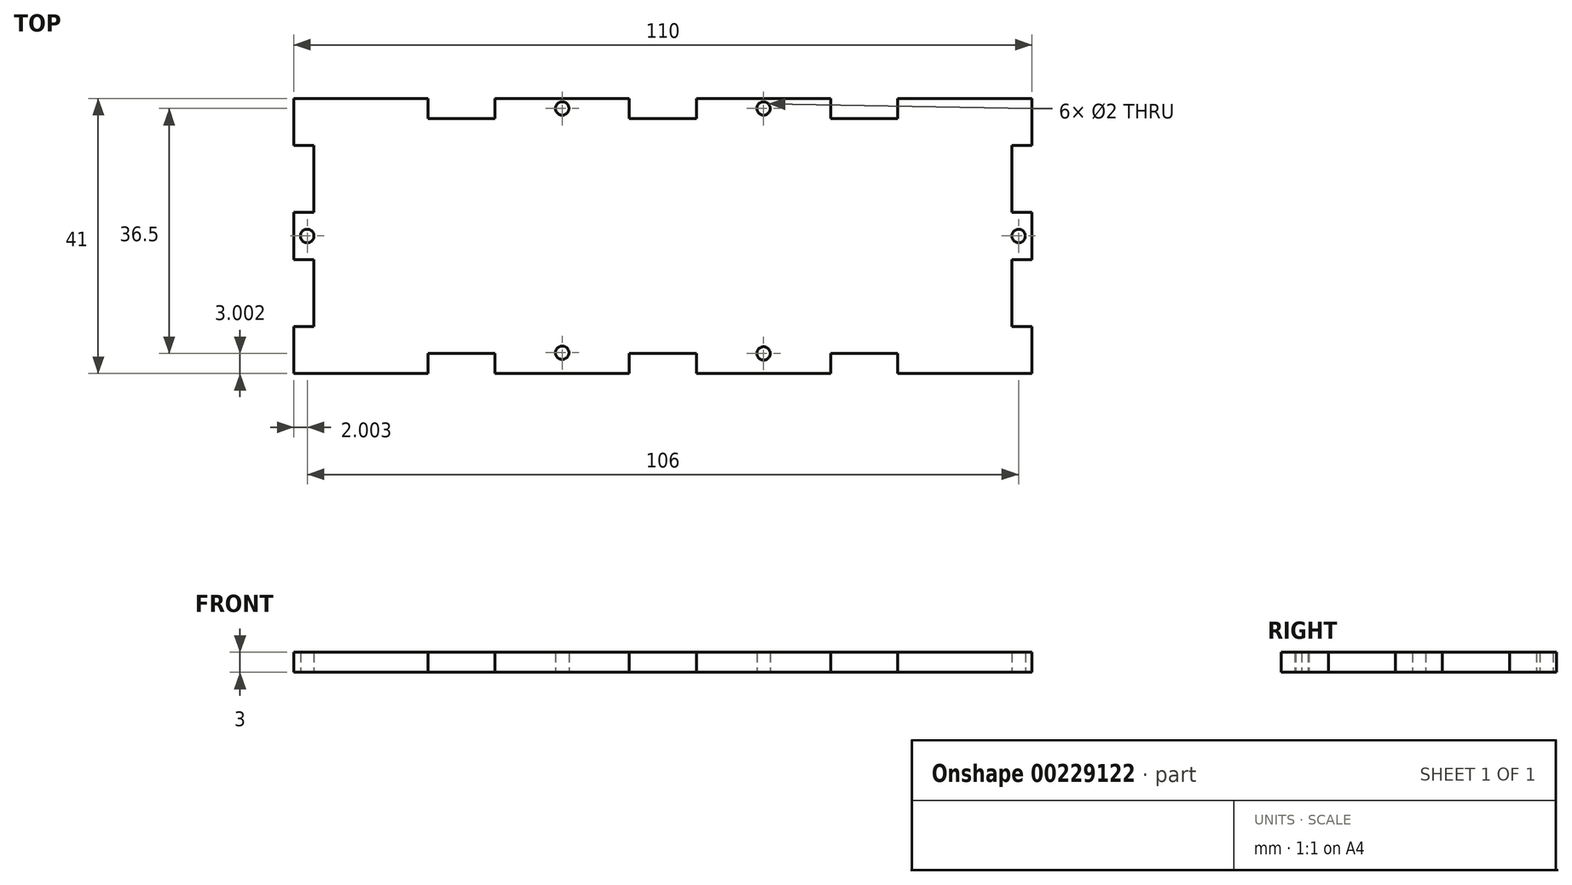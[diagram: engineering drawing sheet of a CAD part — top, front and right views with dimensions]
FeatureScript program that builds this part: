
annotation { "Feature Type Name" : "Feature", "Feature Type Description" : "" }
export const myFeature = defineFeature(function(context is Context, id is Id, definition is map)
    precondition{}
    {
        {
            var Q0;
            Q0=qCreatedBy(makeId("Top.planeOp"),FACE);
            var sketch = newSketch(context, id + "F0", { "sketchPlane" : qUnion([Q0])});
            skLineSegment(sketch, "E0", {"start": v(-52.05, -22.33) * mm, "end": v(-52.05, -15.33) * mm});
            skLineSegment(sketch, "E1", {"start": v(-52.05, -15.33) * mm, "end": v(-49.05, -15.33) * mm});
            skLineSegment(sketch, "E2", {"start": v(-49.05, -15.33) * mm, "end": v(-49.05, -5.33) * mm});
            skLineSegment(sketch, "E3", {"start": v(-49.05, -5.33) * mm, "end": v(-52.05, -5.33) * mm});
            skLineSegment(sketch, "E4", {"start": v(-52.05, -5.33) * mm, "end": v(-52.05, 1.67) * mm});
            skLineSegment(sketch, "E5", {"start": v(-52.05, 1.67) * mm, "end": v(-49.05, 1.67) * mm});
            skLineSegment(sketch, "E6", {"start": v(-49.05, 1.67) * mm, "end": v(-49.05, 11.67) * mm});
            skLineSegment(sketch, "E7", {"start": v(-49.05, 11.67) * mm, "end": v(-52.05, 11.67) * mm});
            skLineSegment(sketch, "E8", {"start": v(-52.05, 11.67) * mm, "end": v(-52.05, 18.67) * mm});
            skLineSegment(sketch, "E9", {"start": v(-52.05, -22.33) * mm, "end": v(-32.05, -22.33) * mm});
            skLineSegment(sketch, "E10", {"start": v(-32.05, -22.33) * mm, "end": v(-32.05, -19.33) * mm});
            skLineSegment(sketch, "E11", {"start": v(-32.05, -19.33) * mm, "end": v(-22.05, -19.33) * mm});
            skLineSegment(sketch, "E12", {"start": v(-22.05, -19.33) * mm, "end": v(-22.05, -22.33) * mm});
            skLineSegment(sketch, "E13", {"start": v(-22.05, -22.33) * mm, "end": v(-2.05, -22.33) * mm});
            skLineSegment(sketch, "E14", {"start": v(-2.05, -22.33) * mm, "end": v(-2.05, -19.33) * mm});
            skLineSegment(sketch, "E15", {"start": v(-2.05, -19.33) * mm, "end": v(2.95, -19.33) * mm});
            skLineSegment(sketch, "E16", {"start": v(-52.05, -1.83) * mm, "end": v(2.95, -1.83) * mm, "construction": true});
            skLineSegment(sketch, "E17.MirrorCS", {"start": v(-22.05, 15.67) * mm, "end": v(-22.05, 18.67) * mm});
            skLineSegment(sketch, "E18.MirrorCS", {"start": v(-32.05, 15.67) * mm, "end": v(-22.05, 15.67) * mm});
            skLineSegment(sketch, "E19.MirrorCS", {"start": v(-32.05, 18.67) * mm, "end": v(-32.05, 15.67) * mm});
            skLineSegment(sketch, "E20.MirrorCS", {"start": v(-2.05, 15.67) * mm, "end": v(2.95, 15.67) * mm});
            skLineSegment(sketch, "E21.MirrorCS", {"start": v(-52.05, 18.67) * mm, "end": v(-32.05, 18.67) * mm});
            skLineSegment(sketch, "E22.MirrorCS", {"start": v(-2.05, 18.67) * mm, "end": v(-2.05, 15.67) * mm});
            skLineSegment(sketch, "E23.MirrorCS", {"start": v(-22.05, 18.67) * mm, "end": v(-2.05, 18.67) * mm});
            skLineSegment(sketch, "E24", {"start": v(2.95, 15.67) * mm, "end": v(2.95, -19.33) * mm, "construction": true});
            skCircle(sketch, "E25", {"center": v(-50.05, -1.83) * mm, "radius": 1 * mm});
            skPoint(sketch, "E26.centerSnap0", {"position": v(-12.05, 18.67) * mm});
            skPoint(sketch, "E26.centerSnap1", {"position": v(-2.05, 17.17) * mm});
            skCircle(sketch, "E27", {"center": v(-12.05, 17.17) * mm, "radius": 1 * mm});
            skLineSegment(sketch, "E28.MirrorCS", {"start": v(37.95, -22.33) * mm, "end": v(37.95, -19.33) * mm});
            skLineSegment(sketch, "E29.MirrorCS", {"start": v(27.95, 15.67) * mm, "end": v(27.95, 18.67) * mm});
            skLineSegment(sketch, "E30.MirrorCS", {"start": v(37.95, 18.67) * mm, "end": v(37.95, 15.67) * mm});
            skLineSegment(sketch, "E31.MirrorCS", {"start": v(57.95, 1.67) * mm, "end": v(54.95, 1.67) * mm});
            skLineSegment(sketch, "E32.MirrorCS", {"start": v(57.95, -15.33) * mm, "end": v(54.95, -15.33) * mm});
            skLineSegment(sketch, "E33.MirrorCS", {"start": v(54.95, 11.67) * mm, "end": v(57.95, 11.67) * mm});
            skLineSegment(sketch, "E34.MirrorCS", {"start": v(54.95, -5.33) * mm, "end": v(57.95, -5.33) * mm});
            skLineSegment(sketch, "E35.MirrorCS", {"start": v(7.95, 18.67) * mm, "end": v(7.95, 15.67) * mm});
            skLineSegment(sketch, "E36.MirrorCS", {"start": v(27.95, -19.33) * mm, "end": v(27.95, -22.33) * mm});
            skLineSegment(sketch, "E37.MirrorCS", {"start": v(7.95, -22.33) * mm, "end": v(7.95, -19.33) * mm});
            skCircle(sketch, "E38.MirrorC", {"center": v(17.95, 17.17) * mm, "radius": 1 * mm});
            skCircle(sketch, "E39.MirrorC", {"center": v(55.95, -1.83) * mm, "radius": 1 * mm});
            skLineSegment(sketch, "E40.MirrorCS", {"start": v(57.95, 11.67) * mm, "end": v(57.95, 18.67) * mm});
            skLineSegment(sketch, "E41.MirrorCS", {"start": v(57.95, 18.67) * mm, "end": v(37.95, 18.67) * mm});
            skLineSegment(sketch, "E42.MirrorCS", {"start": v(57.95, -22.33) * mm, "end": v(37.95, -22.33) * mm});
            skLineSegment(sketch, "E43.MirrorCS", {"start": v(37.95, -19.33) * mm, "end": v(27.95, -19.33) * mm});
            skPoint(sketch, "E44.MirrorP", {"position": v(7.95, 17.17) * mm});
            skLineSegment(sketch, "E45.MirrorCS", {"start": v(54.95, -15.33) * mm, "end": v(54.95, -5.33) * mm});
            skLineSegment(sketch, "E46.MirrorCS", {"start": v(37.95, 15.67) * mm, "end": v(27.95, 15.67) * mm});
            skLineSegment(sketch, "E47.MirrorCS", {"start": v(27.95, 18.67) * mm, "end": v(7.95, 18.67) * mm});
            skLineSegment(sketch, "E48.MirrorCS", {"start": v(57.95, -22.33) * mm, "end": v(57.95, -15.33) * mm});
            skLineSegment(sketch, "E49.MirrorCS", {"start": v(57.95, -5.33) * mm, "end": v(57.95, 1.67) * mm});
            skLineSegment(sketch, "E50.MirrorCS", {"start": v(7.95, -19.33) * mm, "end": v(2.95, -19.33) * mm});
            skLineSegment(sketch, "E51.MirrorCS", {"start": v(27.95, -22.33) * mm, "end": v(7.95, -22.33) * mm});
            skPoint(sketch, "E52.MirrorP", {"position": v(17.95, 18.67) * mm});
            skLineSegment(sketch, "E53.MirrorCS", {"start": v(7.95, 15.67) * mm, "end": v(2.95, 15.67) * mm});
            skLineSegment(sketch, "E54.MirrorCS", {"start": v(54.95, 1.67) * mm, "end": v(54.95, 11.67) * mm});
            skLineSegment(sketch, "E55.MirrorCS", {"start": v(57.95, -1.83) * mm, "end": v(2.95, -1.83) * mm, "construction": true});
            skPoint(sketch, "E56.centerSnap0", {"position": v(-49.05, 6.67) * mm});
            skPoint(sketch, "E56.centerSnap1", {"position": v(-27.05, -19.33) * mm});
            skPoint(sketch, "E57.centerSnap0", {"position": v(-49.05, -10.33) * mm});
            skPoint(sketch, "E57.centerSnap1", {"position": v(-27.05, 15.67) * mm});
            skCircle(sketch, "E58", {"center": v(-12.05, -19.23) * mm, "radius": 1 * mm});
            skPoint(sketch, "E58.centerSnap0", {"position": v(-12.05, -22.33) * mm});
            skCircle(sketch, "E59", {"center": v(17.95, -19.33) * mm, "radius": 1 * mm});
            skPoint(sketch, "E59.centerSnap0", {"position": v(17.95, -22.33) * mm});
            skPoint(sketch, "E59.centerSnap1", {"position": v(5.45, -19.33) * mm});
            skSolve(sketch);
        }
        {
            var Q0;
            Q0 = qSketchRegion(id + "F0", true);
            extrude(context, id + "F1", {"entities" : qUnion([Q0]), "depth" : 3 * mm});
        }
    });
